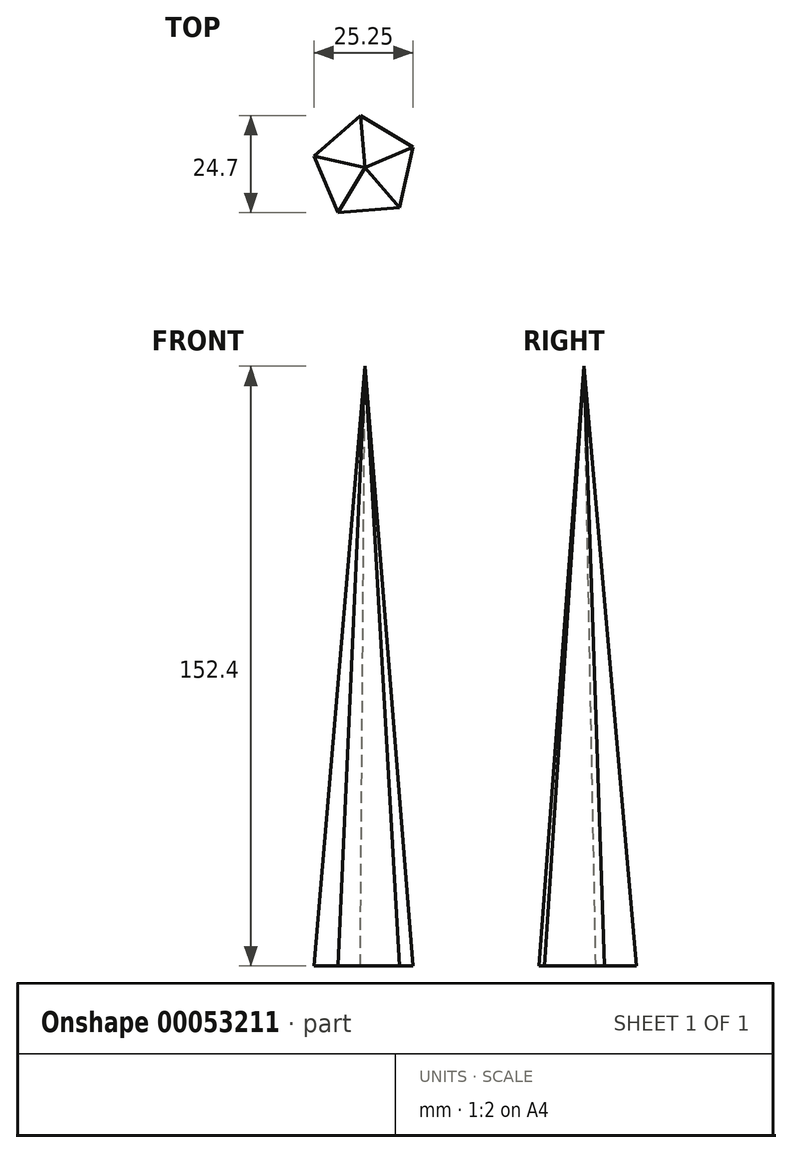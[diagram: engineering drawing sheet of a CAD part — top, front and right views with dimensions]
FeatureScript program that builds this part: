
annotation { "Feature Type Name" : "Feature", "Feature Type Description" : "" }
export const myFeature = defineFeature(function(context is Context, id is Id, definition is map)
    precondition{}
    {
        {
            var Q0;
            Q0=qCreatedBy(makeId("Top.planeOp"),FACE);
            var sketch = newSketch(context, id + "F0", { "sketchPlane" : qUnion([Q0])});
            skCircle(sketch, "E0.cCircle", {"center": v(0, 0) * mm, "radius": 10.78 * mm, "construction": true});
            skLineSegment(sketch, "E0.0", {"start": v(12.27, 5.2) * mm, "end": v(8.74, -10.06) * mm});
            skLineSegment(sketch, "E0.1", {"start": v(8.74, -10.06) * mm, "end": v(-6.86, -11.42) * mm});
            skLineSegment(sketch, "E0.2", {"start": v(-6.86, -11.42) * mm, "end": v(-12.98, 3) * mm});
            skLineSegment(sketch, "E0.3", {"start": v(-12.98, 3) * mm, "end": v(-1.16, 13.28) * mm});
            skLineSegment(sketch, "E0.4", {"start": v(-1.16, 13.28) * mm, "end": v(12.27, 5.2) * mm});
            skPoint(sketch, "E0.0.midPoint", {"position": v(10.5, -2.43) * mm});
            skSolve(sketch);
        }
        {
            var Q0;
            Q0=qCreatedBy(makeId("Top.planeOp"),FACE);
            cPlane(context, id + "F1", {"entities" : qUnion([Q0]), "cplaneType" : CPlaneType.OFFSET, "offset" : 152.4 * mm, "width" : 152.4 * mm, "height" : 152.4 * mm});
        }
        {
            var Q0;
            Q0=qCreatedBy(id+"F1.planeOp",FACE);
            var sketch = newSketch(context, id + "F2", { "sketchPlane" : qUnion([Q0])});
            skPoint(sketch, "E1", {"position": v(0, 0) * mm});
            skSolve(sketch);
        }
        {
            var Q0;
            Q0 = qConstructionFilter(qBodyType(qCreatedBy(id + "F0" ,EDGE), BodyType.WIRE), ConstructionObject.NO);
            var Q1;
            Q1=sQuery(id+"F2.wireOp",VERTEX,"E1");
            loft(context, id + "F3", {"bodyType" : ToolBodyType.SURFACE, "wireProfilesArray" : [{ "wireProfileEntities" : qUnion([Q0]) }, { "wireProfileEntities" : qUnion([Q1]) }]});
        }
    });
